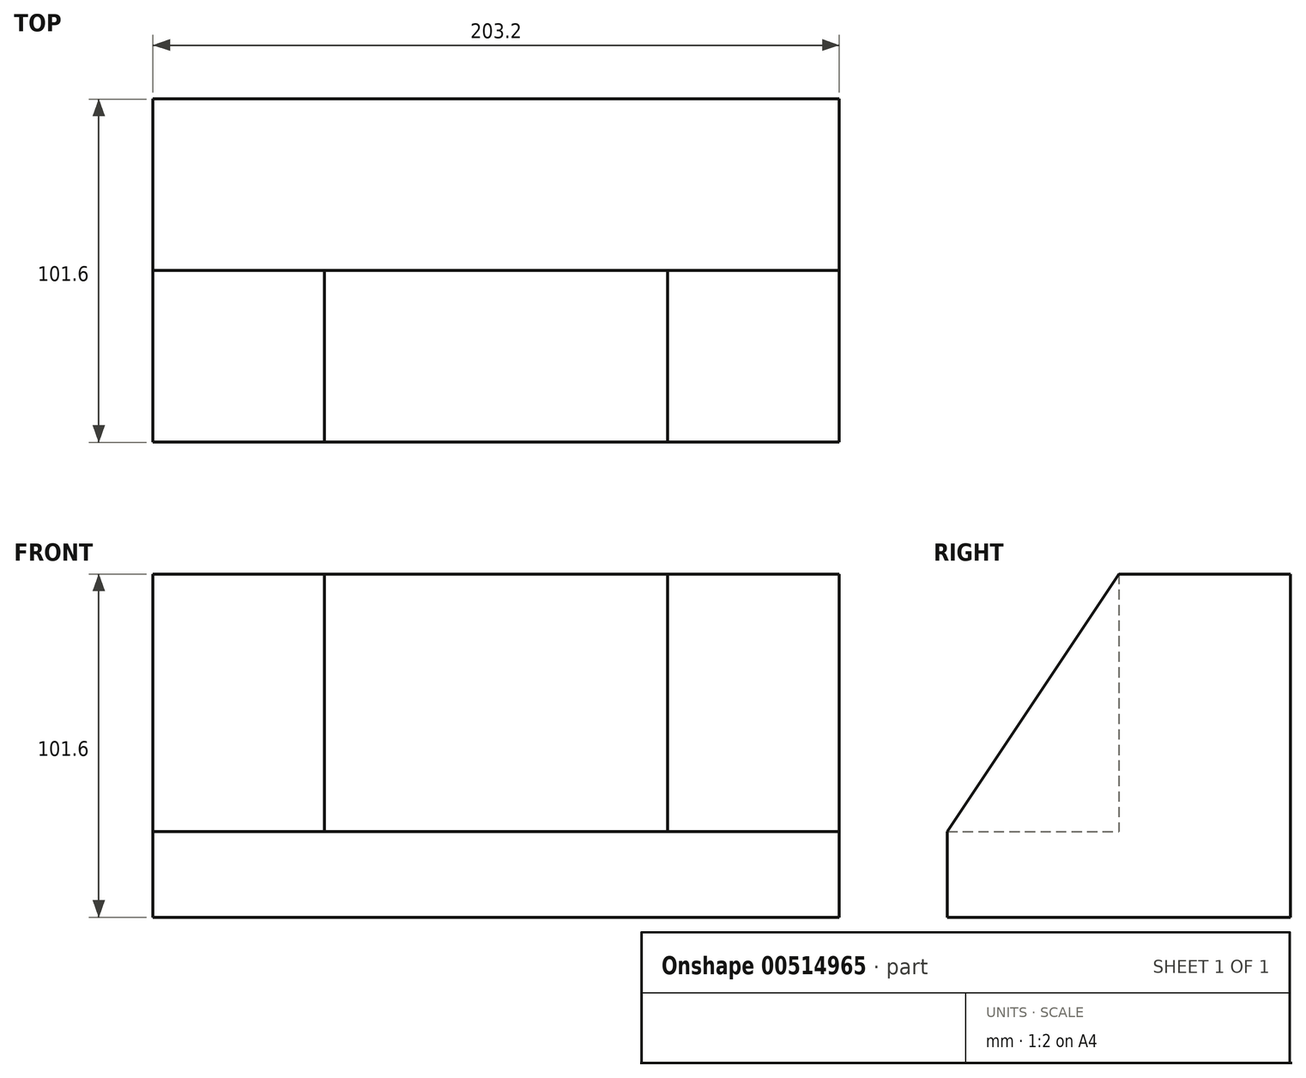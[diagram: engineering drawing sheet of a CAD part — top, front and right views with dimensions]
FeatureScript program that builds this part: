
annotation { "Feature Type Name" : "Feature", "Feature Type Description" : "" }
export const myFeature = defineFeature(function(context is Context, id is Id, definition is map)
    precondition{}
    {
        {
            var Q0;
            Q0=qCreatedBy(makeId("Right.planeOp"),FACE);
            var sketch = newSketch(context, id + "F0", { "sketchPlane" : qUnion([Q0])});
            skLineSegment(sketch, "E0.bottom", {"start": v(43.42, -16.99) * mm, "end": v(-58.18, -16.99) * mm});
            skLineSegment(sketch, "E0.top", {"start": v(43.42, 84.61) * mm, "end": v(-7.38, 84.61) * mm});
            skLineSegment(sketch, "E0.left", {"start": v(43.42, -16.99) * mm, "end": v(43.42, 84.61) * mm});
            skLineSegment(sketch, "E0.right", {"start": v(-58.18, -16.99) * mm, "end": v(-58.18, 8.41) * mm});
            skLineSegment(sketch, "E1", {"start": v(-7.38, 84.61) * mm, "end": v(-58.18, 8.41) * mm});
            skSolve(sketch);
        }
        {
            var Q0;
            Q0 = qSketchRegion(id + "F0", true);
            extrude(context, id + "F1", {"entities" : qUnion([Q0]), "depth" : 203.2 * mm, "offsetDistance" : 25.4 * mm});
        }
        {
            var Q0;
            Q0=makeQuery(id+"F1.opExtrude","SWEPT_FACE",FACE,{"disambiguationData":[OSD([sQuery(id+"F0.wireOp",EDGE,"E0.bottom")])]});
            var sketch = newSketch(context, id + "F2", { "sketchPlane" : qUnion([Q0])});
            skLineSegment(sketch, "E2.bottom", {"start": v(50.8, 58.18) * mm, "end": v(152.4, 58.18) * mm});
            skLineSegment(sketch, "E2.top", {"start": v(50.8, 7.38) * mm, "end": v(152.4, 7.38) * mm});
            skLineSegment(sketch, "E2.left", {"start": v(50.8, 58.18) * mm, "end": v(50.8, 7.38) * mm});
            skLineSegment(sketch, "E2.right", {"start": v(152.4, 58.18) * mm, "end": v(152.4, 7.38) * mm});
            skSolve(sketch);
        }
        {
            var Q0;
            Q0 = qSketchRegion(id + "F2", true);
            extrude(context, id + "F3", {"entities" : qUnion([Q0]), "operationType" : NewBodyOperationType.REMOVE, "oppositeDirection" : true, "depth" : 101.6 * mm, "offsetDistance" : 25.4 * mm});
        }
        {
            var Q0;
            Q0=makeQuery(id+"F3.boolean.opBoolean","COPY",FACE,{"derivedFrom":makeQuery(id+"F3.opExtrude","SWEPT_FACE",FACE,{"disambiguationData":[OSD([sQuery(id+"F2.wireOp",EDGE,"E2.top")])]})});
            var sketch = newSketch(context, id + "F4", { "sketchPlane" : qUnion([Q0])});
            skLineSegment(sketch, "E3.bottom", {"start": v(50.8, -16.99) * mm, "end": v(152.4, -16.99) * mm});
            skLineSegment(sketch, "E3.top", {"start": v(50.8, 8.41) * mm, "end": v(152.4, 8.41) * mm});
            skLineSegment(sketch, "E3.left", {"start": v(50.8, -16.99) * mm, "end": v(50.8, 8.41) * mm});
            skLineSegment(sketch, "E3.right", {"start": v(152.4, -16.99) * mm, "end": v(152.4, 8.41) * mm});
            skSolve(sketch);
        }
        {
            var Q0;
            Q0 = qSketchRegion(id + "F4", true);
            extrude(context, id + "F5", {"entities" : qUnion([Q0]), "operationType" : NewBodyOperationType.ADD, "depth" : 50.8 * mm, "offsetDistance" : 25.4 * mm});
        }
        {
            var Q0;
            Q0 = qSketchRegion(id + "F4", true);
            extrude(context, id + "F6", {"entities" : qUnion([Q0]), "operationType" : NewBodyOperationType.ADD, "depth" : 50.8 * mm, "offsetDistance" : 25.4 * mm});
        }
    });
